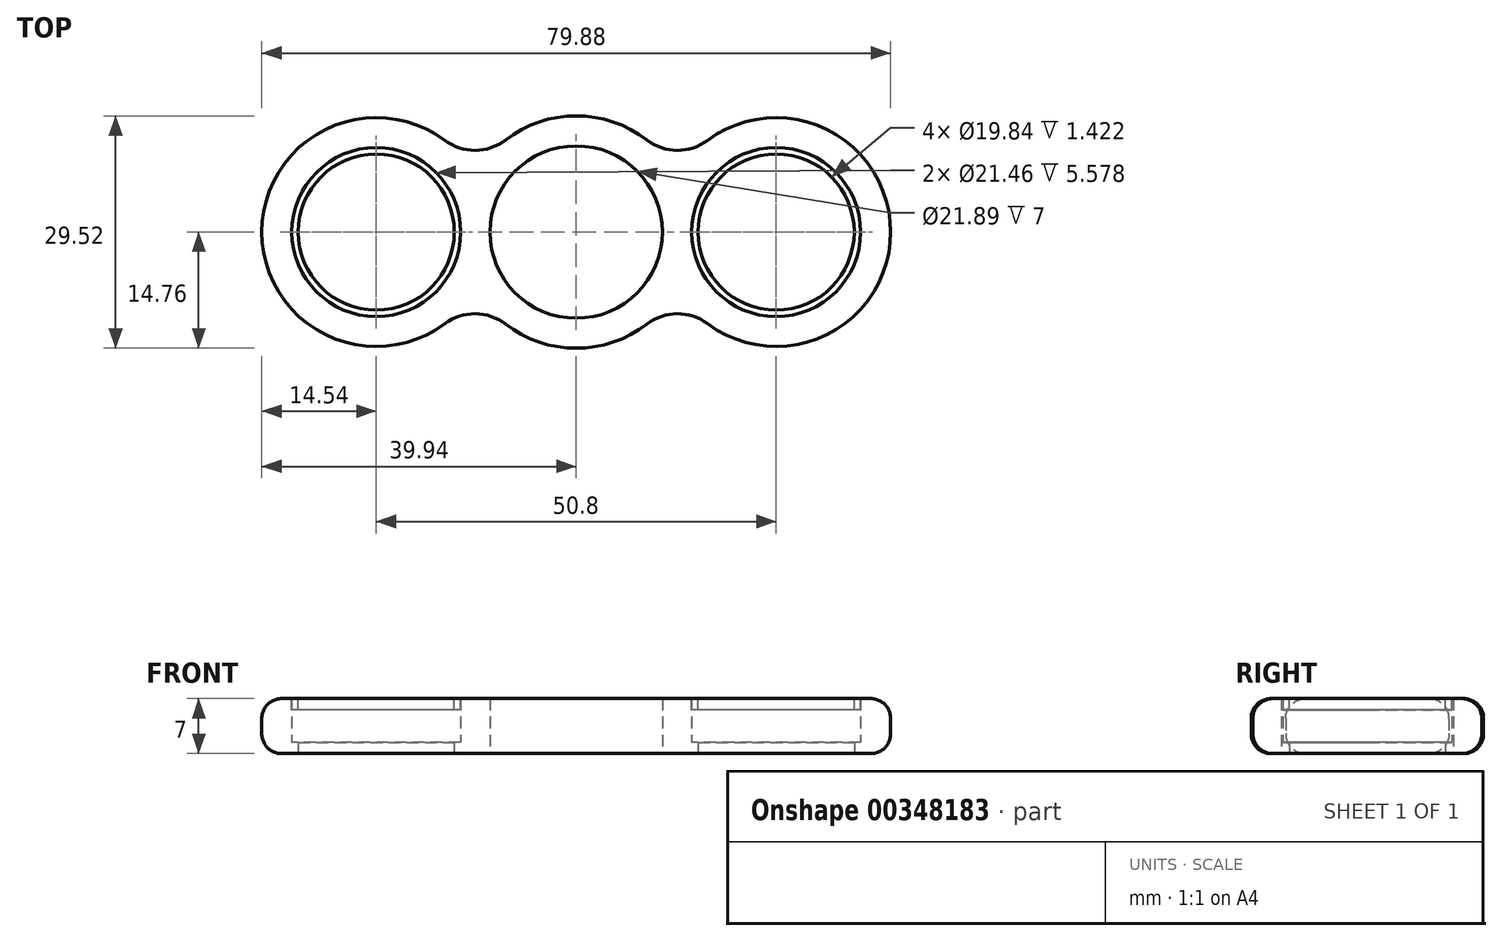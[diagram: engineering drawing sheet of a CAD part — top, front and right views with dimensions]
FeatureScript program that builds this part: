
annotation { "Feature Type Name" : "Feature", "Feature Type Description" : "" }
export const myFeature = defineFeature(function(context is Context, id is Id, definition is map)
    precondition{}
    {
        {
            var Q0;
            Q0=qCreatedBy(makeId("Top.planeOp"),FACE);
            var sketch = newSketch(context, id + "F0", { "sketchPlane" : qUnion([Q0])});
            skCircle(sketch, "E0", {"center": v(0, 0) * mm, "radius": 10.95 * mm});
            skCircle(sketch, "E1", {"center": v(-25.4, 0) * mm, "radius": 10.73 * mm});
            skCircle(sketch, "E2", {"center": v(25.4, 0) * mm, "radius": 10.73 * mm});
            skArc(sketch, "E3.0", {"start": v(-16.68, 11.64) * mm, "mid": v(-39.94, 0) * mm, "end": v(-16.68, -11.64) * mm});
            skArc(sketch, "E4.0", {"start": v(16.68, -11.64) * mm, "mid": v(39.94, 0) * mm, "end": v(16.68, 11.64) * mm});
            skArc(sketch, "E5.0", {"start": v(-9, -11.7) * mm, "mid": v(0, -14.76) * mm, "end": v(9, -11.7) * mm});
            skArc(sketch, "E6.trimOffspring", {"start": v(9, 11.7) * mm, "mid": v(0, 14.76) * mm, "end": v(-9, 11.7) * mm});
            skPoint(sketch, "E7.visualSharp", {"position": v(-12.82, 7.3) * mm});
            skArc(sketch, "E7.filletArc", {"start": v(-16.68, 11.64) * mm, "mid": v(-12.84, 10.37) * mm, "end": v(-9, 11.7) * mm});
            skPoint(sketch, "E8.visualSharp", {"position": v(12.82, 7.3) * mm});
            skArc(sketch, "E8.filletArc", {"start": v(9, 11.7) * mm, "mid": v(12.84, 10.37) * mm, "end": v(16.68, 11.64) * mm});
            skPoint(sketch, "E9.visualSharp", {"position": v(12.82, -7.3) * mm});
            skArc(sketch, "E9.filletArc", {"start": v(16.68, -11.64) * mm, "mid": v(12.84, -10.37) * mm, "end": v(9, -11.7) * mm});
            skPoint(sketch, "E10.visualSharp", {"position": v(-12.82, -7.3) * mm});
            skArc(sketch, "E10.filletArc", {"start": v(-9, -11.7) * mm, "mid": v(-12.84, -10.37) * mm, "end": v(-16.68, -11.64) * mm});
            skSolve(sketch);
        }
        {
            var Q0;
            Q0 = qSketchRegion(id + "F0", true);
            extrude(context, id + "F1", {"entities" : qUnion([Q0]), "depth" : 7 * mm});
        }
        {
            var Q0;
            Q0=makeQuery(id+"F1.opExtrude","CAP_FACE",FACE,{"disambiguationData":[OSD([sQuery(id+"F0.wireOp",EDGE,"E0"),sQuery(id+"F0.wireOp",EDGE,"E1"),sQuery(id+"F0.wireOp",EDGE,"E2"),sQuery(id+"F0.wireOp",EDGE,"E3.0"),sQuery(id+"F0.wireOp",EDGE,"E4.0"),sQuery(id+"F0.wireOp",EDGE,"E5.0"),sQuery(id+"F0.wireOp",EDGE,"E6.trimOffspring"),sQuery(id+"F0.wireOp",EDGE,"E7.filletArc"),sQuery(id+"F0.wireOp",EDGE,"E8.filletArc"),sQuery(id+"F0.wireOp",EDGE,"E9.filletArc"),sQuery(id+"F0.wireOp",EDGE,"E10.filletArc")])],"isStart":false});
            var sketch = newSketch(context, id + "F2", { "sketchPlane" : qUnion([Q0])});
            skCircle(sketch, "E11.0", {"center": v(-25.4, 0) * mm, "radius": 10.73 * mm});
            skCircle(sketch, "E12.0", {"center": v(25.4, 0) * mm, "radius": 10.73 * mm});
            skCircle(sketch, "E13.0", {"center": v(-25.4, 0) * mm, "radius": 9.92 * mm});
            skCircle(sketch, "E14.0", {"center": v(25.4, 0) * mm, "radius": 9.92 * mm});
            skSolve(sketch);
        }
        {
            var Q0;
            Q0 = qSketchRegion(id + "F2", true);
            extrude(context, id + "F3", {"entities" : qUnion([Q0]), "oppositeDirection" : true, "depth" : 1.42 * mm});
        }
        {
            var Q0;
            Q0=makeQuery(id+"F1.opExtrude","CAP_FACE",FACE,{"disambiguationData":[OSD([sQuery(id+"F0.wireOp",EDGE,"E0"),sQuery(id+"F0.wireOp",EDGE,"E1"),sQuery(id+"F0.wireOp",EDGE,"E2"),sQuery(id+"F0.wireOp",EDGE,"E3.0"),sQuery(id+"F0.wireOp",EDGE,"E4.0"),sQuery(id+"F0.wireOp",EDGE,"E5.0"),sQuery(id+"F0.wireOp",EDGE,"E6.trimOffspring"),sQuery(id+"F0.wireOp",EDGE,"E7.filletArc"),sQuery(id+"F0.wireOp",EDGE,"E8.filletArc"),sQuery(id+"F0.wireOp",EDGE,"E9.filletArc"),sQuery(id+"F0.wireOp",EDGE,"E10.filletArc")])],"isStart":true});
            var sketch = newSketch(context, id + "F4", { "sketchPlane" : qUnion([Q0])});
            skCircle(sketch, "E15.0", {"center": v(25.4, 0) * mm, "radius": 10.73 * mm});
            skCircle(sketch, "E16.0", {"center": v(-25.4, 0) * mm, "radius": 10.73 * mm});
            skCircle(sketch, "E17.0", {"center": v(25.4, 0) * mm, "radius": 9.92 * mm});
            skCircle(sketch, "E18.0", {"center": v(-25.4, 0) * mm, "radius": 9.92 * mm});
            skSolve(sketch);
        }
        {
            var Q0;
            Q0 = qSketchRegion(id + "F4", true);
            extrude(context, id + "F5", {"entities" : qUnion([Q0]), "operationType" : NewBodyOperationType.ADD, "oppositeDirection" : true, "depth" : 1.42 * mm});
        }
        {
            var Q0;
            Q0=makeQuery(id+"F1.opExtrude","CAP_EDGE",EDGE,{"disambiguationData":[OSD([sQuery(id+"F0.wireOp",EDGE,"E4.0")])],"isStart":true});
            var Q1;
            Q1=makeQuery(id+"F1.opExtrude","CAP_EDGE",EDGE,{"disambiguationData":[OSD([sQuery(id+"F0.wireOp",EDGE,"E4.0")])],"isStart":false});
            fillet(context, id + "F6", {"entities" : qUnion([Q0, Q1]), "radius" : 2.54 * mm, "tangentPropagation" : true, "allowEdgeOverflow" : false});
        }
    });
